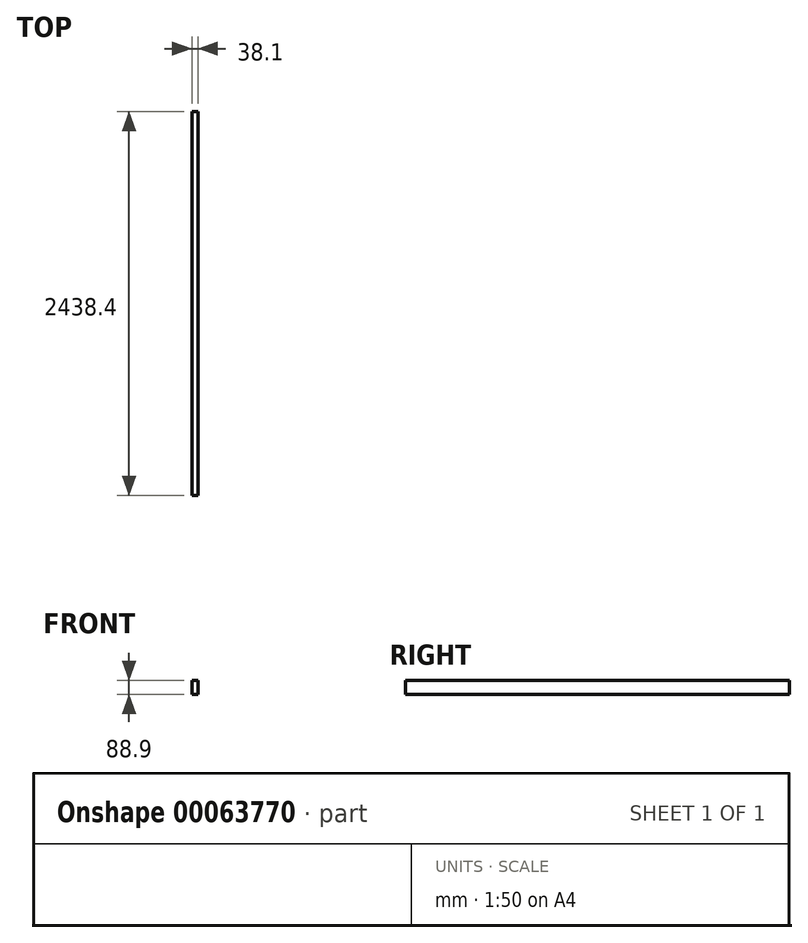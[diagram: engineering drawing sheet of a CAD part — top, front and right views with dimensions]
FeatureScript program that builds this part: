
annotation { "Feature Type Name" : "Feature", "Feature Type Description" : "" }
export const myFeature = defineFeature(function(context is Context, id is Id, definition is map)
    precondition{}
    {
        {
            var Q0;
            Q0=qCreatedBy(makeId("Front.planeOp"),FACE);
            var sketch = newSketch(context, id + "F0", { "sketchPlane" : qUnion([Q0])});
            skLineSegment(sketch, "E0.bottom", {"start": v(-18, 55.77) * mm, "end": v(20.1, 55.77) * mm});
            skLineSegment(sketch, "E0.top", {"start": v(-18, -33.13) * mm, "end": v(20.1, -33.13) * mm});
            skLineSegment(sketch, "E0.left", {"start": v(-18, 55.77) * mm, "end": v(-18, -33.13) * mm});
            skLineSegment(sketch, "E0.right", {"start": v(20.1, 55.77) * mm, "end": v(20.1, -33.13) * mm});
            skSolve(sketch);
        }
        {
            var Q0;
            Q0=qSketchRegion(id+"F0",true);
            extrude(context, id + "F1", {"entities" : qUnion([Q0]), "endBound" : BoundingType.SYMMETRIC, "depth" : 2438.4 * mm});
        }
    });
